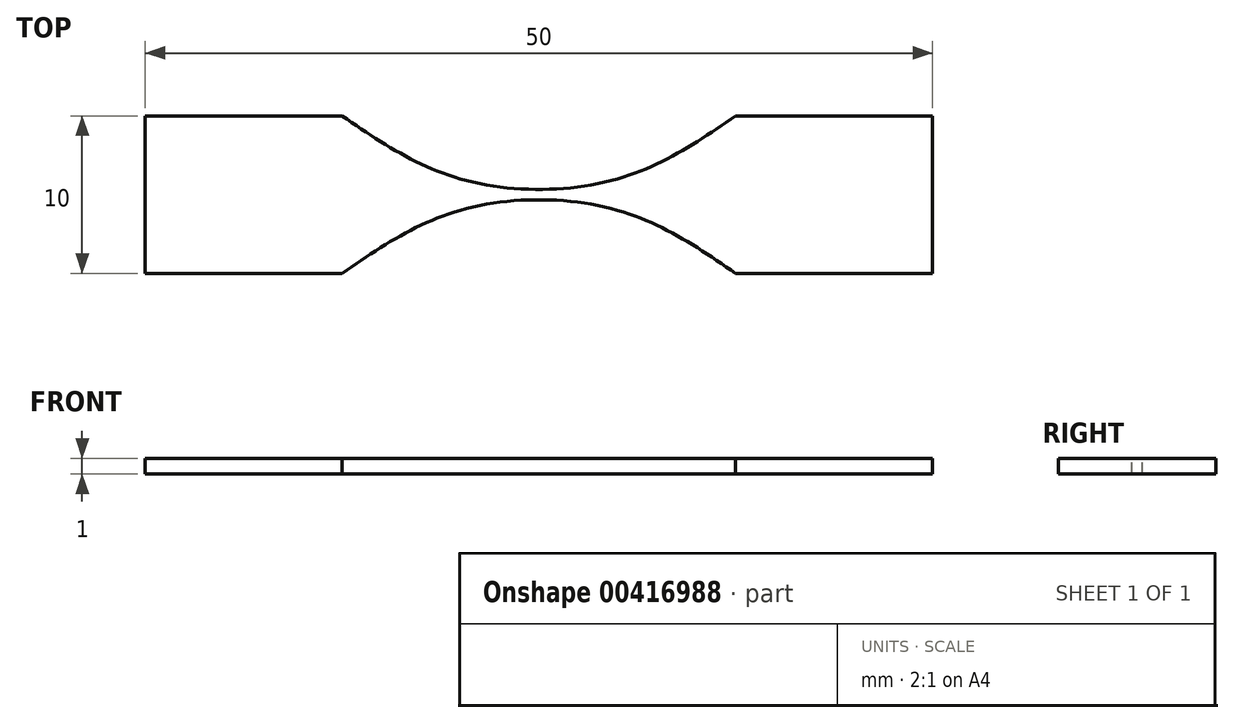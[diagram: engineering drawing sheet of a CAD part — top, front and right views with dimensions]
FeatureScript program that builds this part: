
annotation { "Feature Type Name" : "Feature", "Feature Type Description" : "" }
export const myFeature = defineFeature(function(context is Context, id is Id, definition is map)
    precondition{}
    {
        {
            var Q0;
            Q0=qCreatedBy(makeId("Top.planeOp"),FACE);
            var sketch = newSketch(context, id + "F0", { "sketchPlane" : qUnion([Q0])});
            skLineSegment(sketch, "E0.bottom", {"start": v(-20, 5) * mm, "end": v(-12.5, 5) * mm});
            skLineSegment(sketch, "E0.top", {"start": v(-20, -5) * mm, "end": v(-12.5, -5) * mm});
            skPoint(sketch, "E0.middle", {"position": v(0, 0) * mm});
            skLineSegment(sketch, "E1.bottom", {"start": v(-5, 1) * mm, "end": v(5, 1) * mm});
            skLineSegment(sketch, "E1.top", {"start": v(-5, -1) * mm, "end": v(5, -1) * mm});
            skFitSpline(sketch, "E2", {"points": [v(-12.5, 5) * mm, v(-5, 1) * mm, v(5, 1) * mm, v(12.5, 5) * mm], "startDerivative": vector(21.42, -14.69) * mm, "endDerivative": vector(21.42, 14.69) * mm});
            skFitSpline(sketch, "E3", {"points": [v(12.5, -5) * mm, v(5, -1) * mm, v(-5, -1) * mm, v(-12.5, -5) * mm], "startDerivative": vector(-21.42, 14.69) * mm, "endDerivative": vector(-21.42, -14.69) * mm});
            skFitSpline(sketch, "E4.trimOffspring", {"points": [v(12.5, -5) * mm, v(5, -1) * mm, v(-5, -1) * mm, v(-12.5, -5) * mm], "startDerivative": vector(-21.42, 14.69) * mm, "endDerivative": vector(-21.42, -14.69) * mm});
            skLineSegment(sketch, "E5.trimOffspring", {"start": v(12.5, 5) * mm, "end": v(20, 5) * mm});
            skLineSegment(sketch, "E6.trimOffspring", {"start": v(12.5, -5) * mm, "end": v(20, -5) * mm});
            skLineSegment(sketch, "E7.bottom", {"start": v(-20, 5) * mm, "end": v(-25, 5) * mm});
            skLineSegment(sketch, "E7.top", {"start": v(-20, -5) * mm, "end": v(-25, -5) * mm});
            skLineSegment(sketch, "E7.right", {"start": v(-25, 5) * mm, "end": v(-25, -5) * mm});
            skLineSegment(sketch, "E8.bottom", {"start": v(20, 5) * mm, "end": v(25, 5) * mm});
            skLineSegment(sketch, "E8.top", {"start": v(20, -5) * mm, "end": v(25, -5) * mm});
            skLineSegment(sketch, "E8.right", {"start": v(25, 5) * mm, "end": v(25, -5) * mm});
            skSolve(sketch);
        }
        {
            var Q0;
            Q0=makeQuery(id+"F0.imprint","IMPRINT",FACE,{"disambiguationData":[TD([[makeQuery(id+"F0.imprint","IMPRINT",EDGE,{"derivedFrom":sQuery(id+"F0.wireOp",EDGE,"E0.bottom")}),-1.0]])]});
            extrude(context, id + "F1", {"entities" : qUnion([Q0]), "depth" : 1 * mm});
        }
    });
